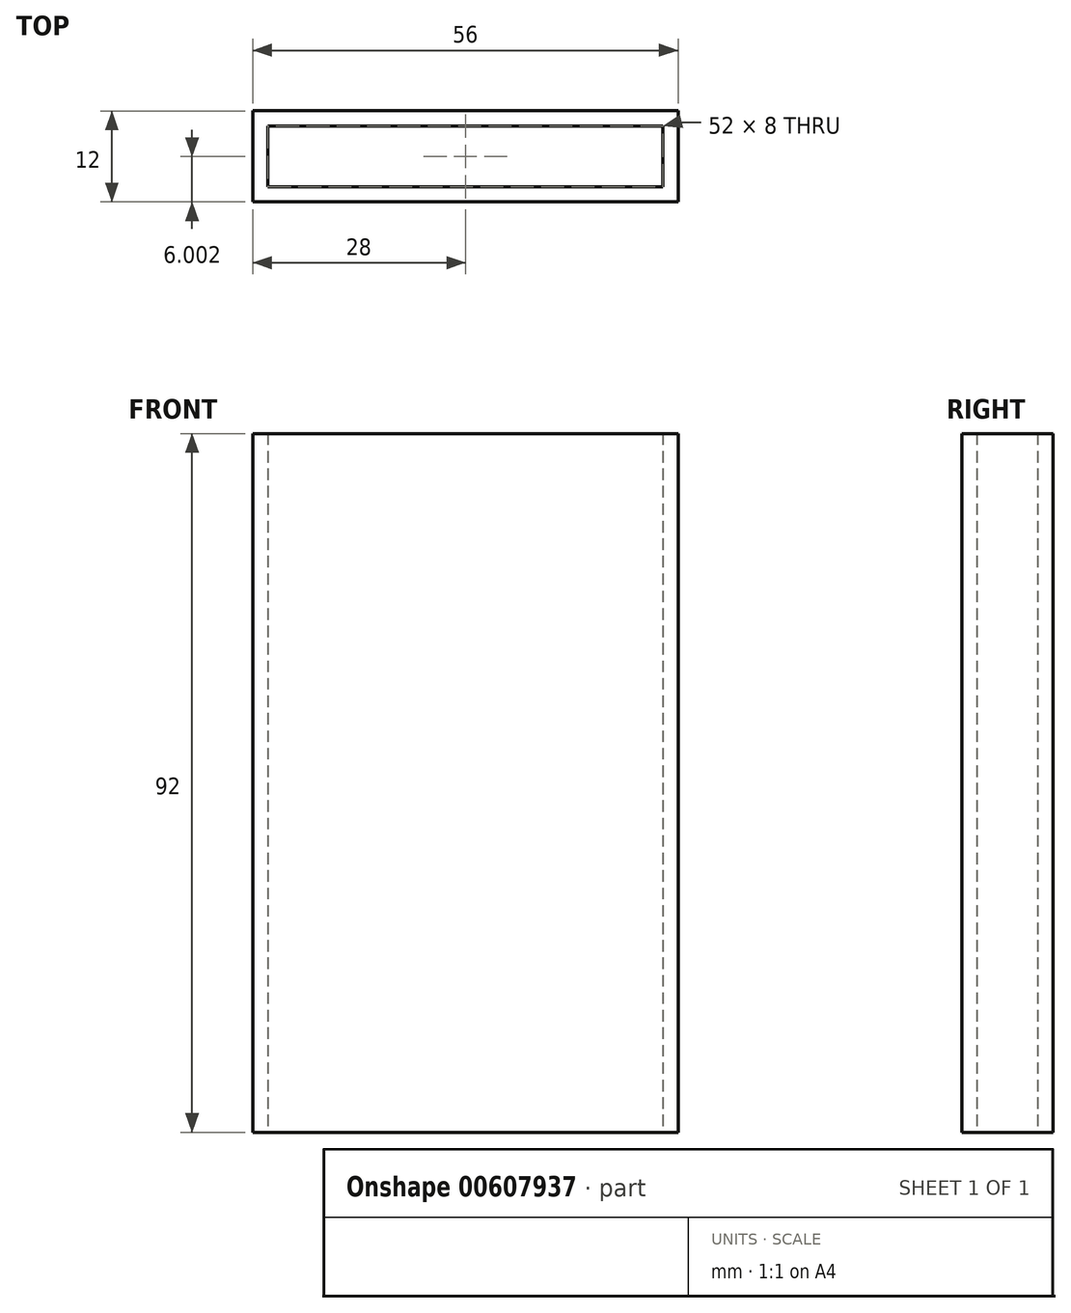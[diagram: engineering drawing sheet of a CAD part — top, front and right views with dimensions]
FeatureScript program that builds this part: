
annotation { "Feature Type Name" : "Feature", "Feature Type Description" : "" }
export const myFeature = defineFeature(function(context is Context, id is Id, definition is map)
    precondition{}
    {
        {
            var Q0;
            Q0=qCreatedBy(makeId("Top.planeOp"),FACE);
            var sketch = newSketch(context, id + "F0", { "sketchPlane" : qUnion([Q0])});
            skLineSegment(sketch, "E0.bottom", {"start": v(-45.41, 23.35) * mm, "end": v(6.59, 23.35) * mm});
            skLineSegment(sketch, "E0.top", {"start": v(-45.41, 15.35) * mm, "end": v(6.59, 15.35) * mm});
            skLineSegment(sketch, "E0.left", {"start": v(-45.41, 23.35) * mm, "end": v(-45.41, 15.35) * mm});
            skLineSegment(sketch, "E0.right", {"start": v(6.59, 23.35) * mm, "end": v(6.59, 15.35) * mm});
            skLineSegment(sketch, "E1.0", {"start": v(-47.41, 25.35) * mm, "end": v(8.59, 25.35) * mm});
            skLineSegment(sketch, "E1.1", {"start": v(-47.41, 25.35) * mm, "end": v(-47.41, 13.35) * mm});
            skLineSegment(sketch, "E1.2", {"start": v(-47.41, 13.35) * mm, "end": v(8.59, 13.35) * mm});
            skLineSegment(sketch, "E1.3", {"start": v(8.59, 25.35) * mm, "end": v(8.59, 13.35) * mm});
            skSolve(sketch);
        }
        {
            var Q0;
            Q0=makeQuery(id+"F0.imprint","IMPRINT",FACE,{"disambiguationData":[TD([[makeQuery(id+"F0.imprint","IMPRINT",EDGE,{"derivedFrom":sQuery(id+"F0.wireOp",EDGE,"E0.bottom")}),1.0]])]});
            extrude(context, id + "F1", {"entities" : qUnion([Q0]), "depth" : 90 * mm, "offsetDistance" : 25 * mm});
        }
        {
            var Q0;
            Q0=makeQuery(id+"F1.opExtrude","CAP_FACE",FACE,{"disambiguationData":[OSD([sQuery(id+"F0.wireOp",EDGE,"E0.bottom"),sQuery(id+"F0.wireOp",EDGE,"E0.top"),sQuery(id+"F0.wireOp",EDGE,"E0.left"),sQuery(id+"F0.wireOp",EDGE,"E0.right"),sQuery(id+"F0.wireOp",EDGE,"E1.0"),sQuery(id+"F0.wireOp",EDGE,"E1.1"),sQuery(id+"F0.wireOp",EDGE,"E1.2"),sQuery(id+"F0.wireOp",EDGE,"E1.3")])],"isStart":false});
            extrude(context, id + "F2", {"entities" : qUnion([Q0]), "operationType" : NewBodyOperationType.ADD, "depth" : 2 * mm, "offsetDistance" : 25 * mm});
        }
    });
